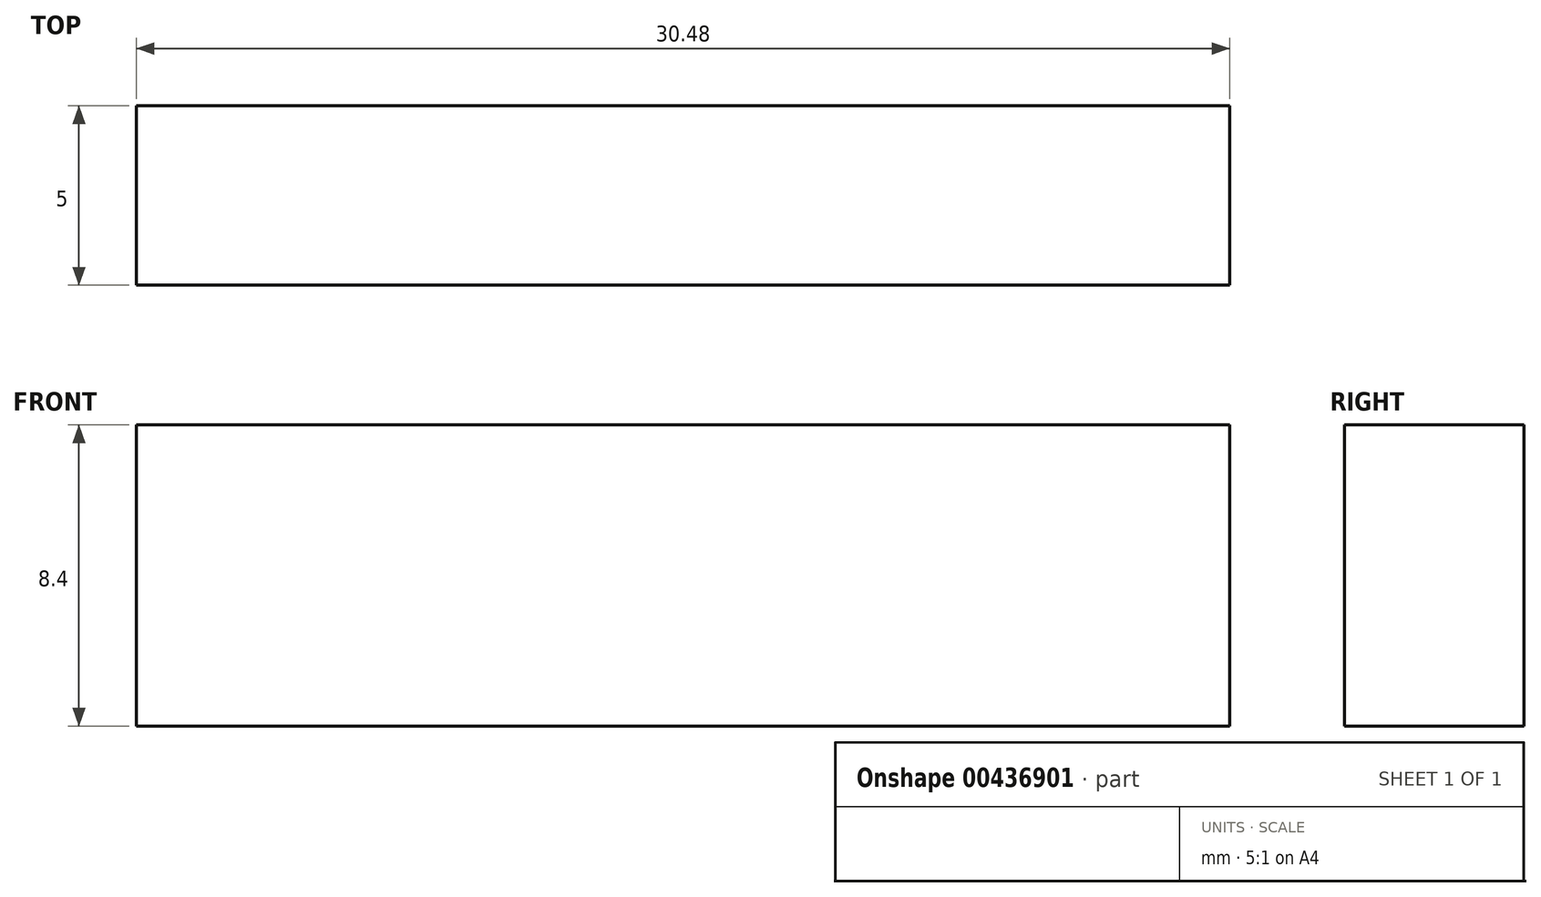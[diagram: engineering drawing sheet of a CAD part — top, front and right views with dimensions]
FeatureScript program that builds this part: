
annotation { "Feature Type Name" : "Feature", "Feature Type Description" : "" }
export const myFeature = defineFeature(function(context is Context, id is Id, definition is map)
    precondition{}
    {
        {
            var Q0;
            Q0=qCreatedBy(makeId("Top.planeOp"),FACE);
            var sketch = newSketch(context, id + "F0", { "sketchPlane" : qUnion([Q0])});
            skLineSegment(sketch, "E0.bottom", {"start": v(0, 0) * mm, "end": v(30.48, 0) * mm});
            skLineSegment(sketch, "E0.top", {"start": v(0, 5) * mm, "end": v(30.48, 5) * mm});
            skLineSegment(sketch, "E0.left", {"start": v(0, 0) * mm, "end": v(0, 5) * mm});
            skLineSegment(sketch, "E0.right", {"start": v(30.48, 0) * mm, "end": v(30.48, 5) * mm});
            skSolve(sketch);
        }
        {
            var Q0;
            Q0 = qSketchRegion(id + "F0", true);
            extrude(context, id + "F1", {"entities" : qUnion([Q0]), "depth" : 8.4 * mm});
        }
    });
